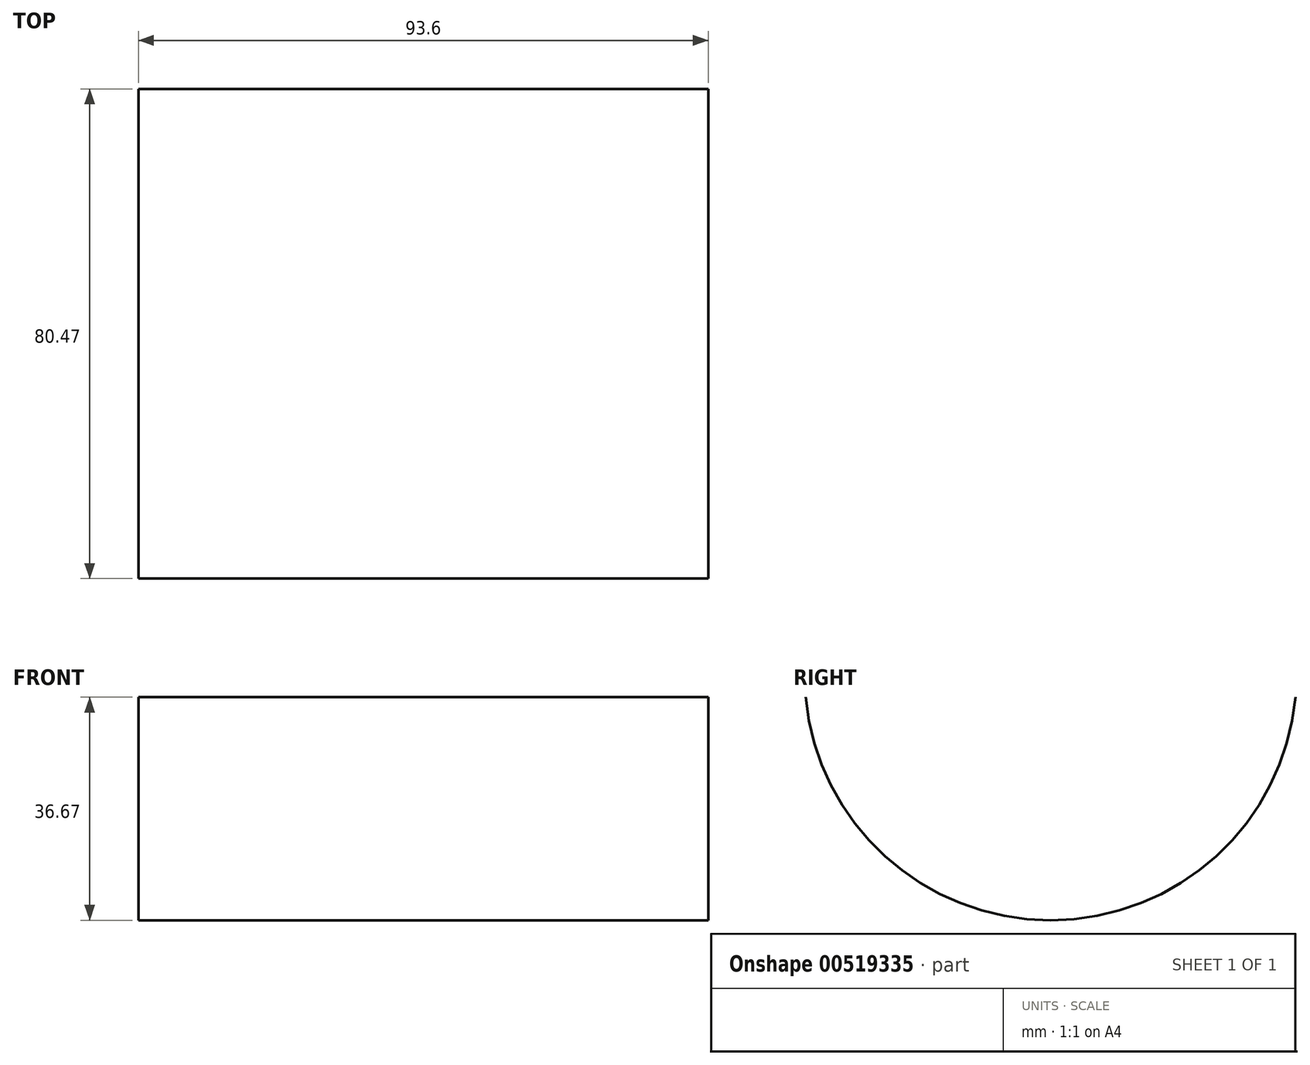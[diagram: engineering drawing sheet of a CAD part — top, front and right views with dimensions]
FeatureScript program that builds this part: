
annotation { "Feature Type Name" : "Feature", "Feature Type Description" : "" }
export const myFeature = defineFeature(function(context is Context, id is Id, definition is map)
    precondition{}
    {
        {
            var Q0;
            Q0=qCreatedBy(makeId("Top.planeOp"),FACE);
            var sketch = newSketch(context, id + "F0", { "sketchPlane" : qUnion([Q0])});
            skLineSegment(sketch, "E0.bottom", {"start": v(-87.91, 33.84) * mm, "end": v(126.48, 33.84) * mm});
            skLineSegment(sketch, "E0.top", {"start": v(-87.91, -86.97) * mm, "end": v(126.48, -86.97) * mm});
            skLineSegment(sketch, "E0.left", {"start": v(-87.91, 33.84) * mm, "end": v(-87.91, -86.97) * mm});
            skLineSegment(sketch, "E0.right", {"start": v(126.48, 33.84) * mm, "end": v(126.48, -86.97) * mm});
            skLineSegment(sketch, "E1.bottom", {"start": v(-68.59, 176.5) * mm, "end": v(126.64, 176.5) * mm});
            skLineSegment(sketch, "E1.top", {"start": v(-68.59, 108.62) * mm, "end": v(126.64, 108.62) * mm});
            skLineSegment(sketch, "E1.left", {"start": v(-68.59, 176.5) * mm, "end": v(-68.59, 108.62) * mm});
            skLineSegment(sketch, "E1.right", {"start": v(126.64, 176.5) * mm, "end": v(126.64, 108.62) * mm});
            skLineSegment(sketch, "E2.bottom", {"start": v(-56.39, -189.77) * mm, "end": v(141.82, -189.77) * mm});
            skLineSegment(sketch, "E2.top", {"start": v(-56.39, -288.7) * mm, "end": v(141.82, -288.7) * mm});
            skLineSegment(sketch, "E2.left", {"start": v(-56.39, -189.77) * mm, "end": v(-56.39, -288.7) * mm});
            skLineSegment(sketch, "E2.right", {"start": v(141.82, -189.77) * mm, "end": v(141.82, -288.7) * mm});
            skLineSegment(sketch, "E3.bottom", {"start": v(-206.6, 88.3) * mm, "end": v(-310.74, 88.3) * mm});
            skLineSegment(sketch, "E3.top", {"start": v(-206.6, -267.79) * mm, "end": v(-310.74, -267.79) * mm});
            skLineSegment(sketch, "E3.left", {"start": v(-206.6, 88.3) * mm, "end": v(-206.6, -267.79) * mm});
            skLineSegment(sketch, "E3.right", {"start": v(-310.74, 88.3) * mm, "end": v(-310.74, -267.79) * mm});
            skSolve(sketch);
        }
        {
            var Q0;
            Q0=qCreatedBy(makeId("Right.planeOp"),FACE);
            var sketch = newSketch(context, id + "F1", { "sketchPlane" : qUnion([Q0])});
            skArc(sketch, "E4", {"start": v(-454.33, 0) * mm, "mid": v(-414.1, -36.67) * mm, "end": v(-373.86, 0) * mm});
            skSolve(sketch);
        }
        {
            var Q0;
            Q0=sQuery(id+"F1.wireOp",EDGE,"E4");
            extrude(context, id + "F2", {"bodyType" : ToolBodyType.SURFACE, "surfaceEntities" : qUnion([Q0]), "depth" : 93.6 * mm, "offsetDistance" : 25.4 * mm});
        }
    });
